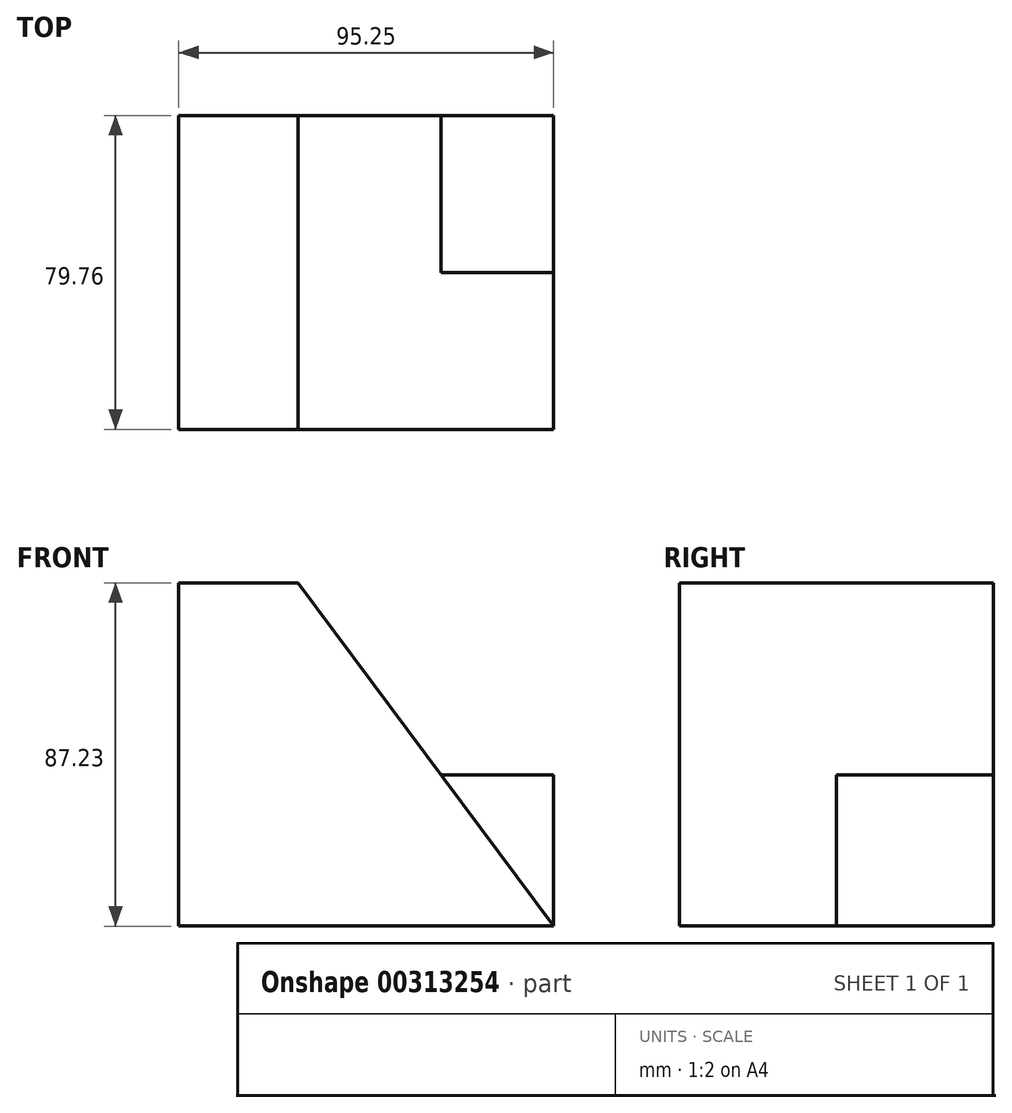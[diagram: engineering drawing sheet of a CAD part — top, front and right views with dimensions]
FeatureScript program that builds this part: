
annotation { "Feature Type Name" : "Feature", "Feature Type Description" : "" }
export const myFeature = defineFeature(function(context is Context, id is Id, definition is map)
    precondition{}
    {
        {
            var Q0;
            Q0=qCreatedBy(makeId("Front.planeOp"),FACE);
            var sketch = newSketch(context, id + "F0", { "sketchPlane" : qUnion([Q0])});
            skLineSegment(sketch, "E0", {"start": v(47.52, -43.92) * mm, "end": v(-47.73, -43.92) * mm});
            skLineSegment(sketch, "E1", {"start": v(-47.73, -43.92) * mm, "end": v(-47.73, 43.31) * mm});
            skLineSegment(sketch, "E2", {"start": v(-47.73, 43.31) * mm, "end": v(-17.45, 43.31) * mm});
            skLineSegment(sketch, "E3", {"start": v(-17.45, 43.31) * mm, "end": v(47.52, -43.92) * mm});
            skSolve(sketch);
        }
        {
            var Q0;
            Q0 = qSketchRegion(id + "F0", true);
            extrude(context, id + "F1", {"entities" : qUnion([Q0]), "depth" : 79.76 * mm});
        }
        {
            var Q0;
            Q0=makeQuery(id+"F1.opExtrude","CAP_FACE",FACE,{"disambiguationData":[OSD([sQuery(id+"F0.wireOp",EDGE,"E0"),sQuery(id+"F0.wireOp",EDGE,"E1"),sQuery(id+"F0.wireOp",EDGE,"E2"),sQuery(id+"F0.wireOp",EDGE,"E3")])],"isStart":true});
            var sketch = newSketch(context, id + "F2", { "sketchPlane" : qUnion([Q0])});
            skLineSegment(sketch, "E4", {"start": v(-47.52, -43.92) * mm, "end": v(-47.52, -5.47) * mm});
            skLineSegment(sketch, "E5", {"start": v(-47.52, -5.47) * mm, "end": v(-18.89, -5.47) * mm});
            skSolve(sketch);
        }
        {
            var Q0;
            {var subQ0=sQuery(id+"F2.wireOp",EDGE,"E4");Q0=makeQuery(id+"F2.imprint","IMPRINT",FACE,{"disambiguationData":[TD([[makeQuery(id+"F2.imprint","IMPRINT",EDGE,{"derivedFrom":subQ0}),-1.0]])]});}
            extrude(context, id + "F3", {"entities" : qUnion([Q0]), "operationType" : NewBodyOperationType.ADD, "oppositeDirection" : true, "depth" : 39.88 * mm});
        }
    });
